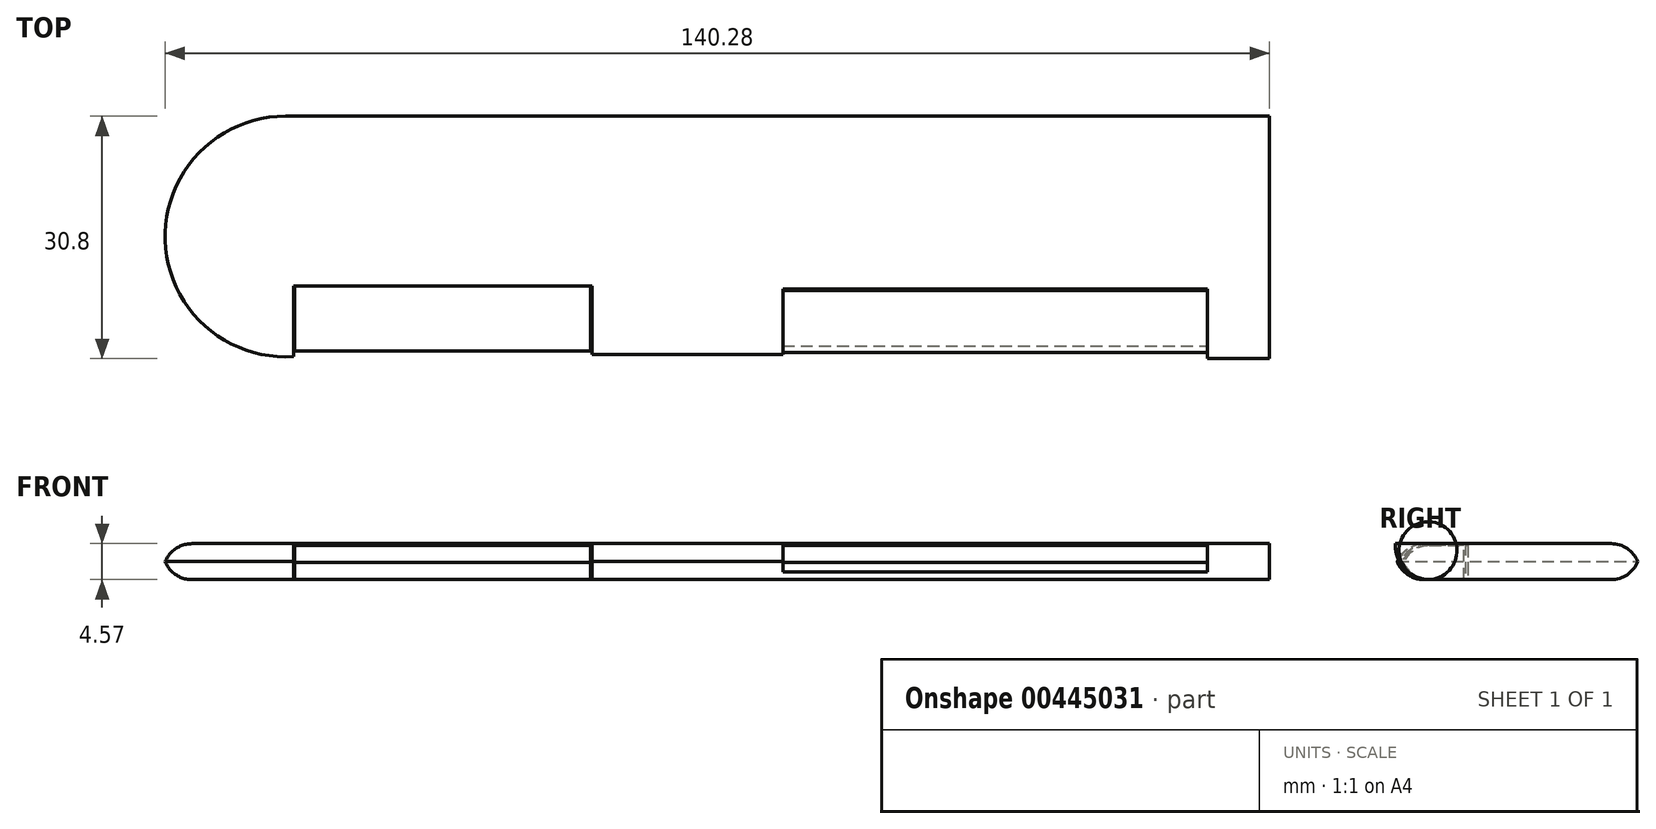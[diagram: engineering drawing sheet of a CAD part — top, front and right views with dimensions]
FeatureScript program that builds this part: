
annotation { "Feature Type Name" : "Feature", "Feature Type Description" : "" }
export const myFeature = defineFeature(function(context is Context, id is Id, definition is map)
    precondition{}
    {
        {
            var Q0;
            Q0=qCreatedBy(makeId("Top.planeOp"),FACE);
            var sketch = newSketch(context, id + "F0", { "sketchPlane" : qUnion([Q0])});
            skLineSegment(sketch, "E0", {"start": v(-60.57, 38.54) * mm, "end": v(53.16, 38.54) * mm});
            skLineSegment(sketch, "E1", {"start": v(53.16, 38.54) * mm, "end": v(53.16, 7.46) * mm});
            skLineSegment(sketch, "E2", {"start": v(53.16, 7.46) * mm, "end": v(45.3, 7.46) * mm});
            skLineSegment(sketch, "E3", {"start": v(45.3, 7.46) * mm, "end": v(45.3, 16.34) * mm});
            skLineSegment(sketch, "E4", {"start": v(45.3, 16.34) * mm, "end": v(-8.65, 16.34) * mm});
            skLineSegment(sketch, "E5", {"start": v(-8.65, 16.34) * mm, "end": v(-8.65, 7.46) * mm});
            skLineSegment(sketch, "E6", {"start": v(-8.65, 7.46) * mm, "end": v(-32.9, 7.46) * mm});
            skLineSegment(sketch, "E7", {"start": v(-32.9, 7.46) * mm, "end": v(-32.9, 16.68) * mm});
            skLineSegment(sketch, "E8", {"start": v(-32.9, 16.68) * mm, "end": v(-70.81, 16.68) * mm});
            skLineSegment(sketch, "E9", {"start": v(-70.81, 16.68) * mm, "end": v(-70.81, 7.46) * mm});
            skLineSegment(sketch, "E10", {"start": v(-60.57, 38.54) * mm, "end": v(-71.84, 38.54) * mm});
            skArc(sketch, "E11", {"start": v(-71.84, 38.54) * mm, "mid": v(-87.38, 22.47) * mm, "end": v(-70.81, 7.46) * mm});
            skSolve(sketch);
        }
        {
            var Q0;
            Q0 = qSketchRegion(id + "F0", true);
            extrude(context, id + "F1", {"entities" : qUnion([Q0]), "depth" : 4.57 * mm});
        }
        {
            var Q0;
            Q0=makeQuery(id+"F1.opExtrude","CAP_EDGE",EDGE,{"disambiguationData":[OSD([sQuery(id+"F0.wireOp",EDGE,"E0"),sQuery(id+"F0.wireOp",EDGE,"E10")])],"isStart":false});
            var Q1;
            Q1=makeQuery(id+"F1.opExtrude","CAP_EDGE",EDGE,{"disambiguationData":[OSD([sQuery(id+"F0.wireOp",EDGE,"E0"),sQuery(id+"F0.wireOp",EDGE,"E10")])],"isStart":true});
            fillet(context, id + "F2", {"entities" : qUnion([Q0, Q1]), "radius" : 3.68 * mm, "tangentPropagation" : true, "allowEdgeOverflow" : false});
        }
        {
            var Q0;
            Q0=qCreatedBy(makeId("Top.planeOp"),FACE);
            var sketch = newSketch(context, id + "F3", { "sketchPlane" : qUnion([Q0])});
            skLineSegment(sketch, "E12.bottom", {"start": v(-70.64, 8.12) * mm, "end": v(-33.07, 8.12) * mm});
            skLineSegment(sketch, "E12.top", {"start": v(-70.64, 16.85) * mm, "end": v(-33.07, 16.85) * mm});
            skLineSegment(sketch, "E12.left", {"start": v(-70.64, 8.12) * mm, "end": v(-70.64, 16.85) * mm});
            skLineSegment(sketch, "E12.right", {"start": v(-33.07, 8.12) * mm, "end": v(-33.07, 16.85) * mm});
            skLineSegment(sketch, "E13.bottom", {"start": v(-8.9, 7.92) * mm, "end": v(45.31, 7.92) * mm});
            skLineSegment(sketch, "E13.top", {"start": v(-8.9, 15.84) * mm, "end": v(45.31, 15.84) * mm});
            skLineSegment(sketch, "E13.left", {"start": v(-8.9, 7.92) * mm, "end": v(-8.9, 15.84) * mm});
            skLineSegment(sketch, "E13.right", {"start": v(45.31, 7.92) * mm, "end": v(45.31, 15.84) * mm});
            skSolve(sketch);
        }
        {
            var Q0;
            Q0=makeQuery(id+"F3.imprint","IMPRINT",FACE,{"disambiguationData":[TD([[makeQuery(id+"F3.imprint","IMPRINT",EDGE,{"derivedFrom":sQuery(id+"F3.wireOp",EDGE,"E12.bottom")}),1.0]])]});
            var Q1;
            Q1=makeQuery(id+"F3.imprint","IMPRINT",FACE,{"disambiguationData":[TD([[makeQuery(id+"F3.imprint","IMPRINT",EDGE,{"derivedFrom":sQuery(id+"F3.wireOp",EDGE,"E13.bottom")}),1.0]])]});
            extrude(context, id + "F4", {"entities" : qUnion([Q0, Q1]), "operationType" : NewBodyOperationType.ADD, "depth" : 4.32 * mm});
        }
        {
            var Q0;
            Q0=makeQuery(id+"F4.opExtrude","CAP_EDGE",EDGE,{"disambiguationData":[OSD([sQuery(id+"F3.wireOp",EDGE,"E12.bottom")])],"isStart":false});
            var Q1;
            Q1=makeQuery(id+"F4.opExtrude","CAP_EDGE",EDGE,{"disambiguationData":[OSD([sQuery(id+"F3.wireOp",EDGE,"E12.bottom")])],"isStart":true});
            var Q2;
            Q2=makeQuery(id+"F4.opExtrude","CAP_EDGE",EDGE,{"disambiguationData":[OSD([sQuery(id+"F3.wireOp",EDGE,"E13.bottom")])],"isStart":true});
            var Q3;
            Q3=makeQuery(id+"F4.opExtrude","CAP_EDGE",EDGE,{"disambiguationData":[OSD([sQuery(id+"F3.wireOp",EDGE,"E13.bottom")])],"isStart":false});
            fillet(context, id + "F5", {"entities" : qUnion([Q0, Q1, Q2, Q3]), "radius" : 3.68 * mm, "tangentPropagation" : true, "allowEdgeOverflow" : false});
        }
        {
            var Q0;
            Q0=makeQuery(id+"F1.opExtrude","CAP_EDGE",EDGE,{"disambiguationData":[OSD([sQuery(id+"F0.wireOp",EDGE,"E6")])],"isStart":true});
            var Q1;
            Q1=makeQuery(id+"F1.opExtrude","CAP_EDGE",EDGE,{"disambiguationData":[OSD([sQuery(id+"F0.wireOp",EDGE,"E6")])],"isStart":false});
            fillet(context, id + "F6", {"entities" : qUnion([Q0, Q1]), "radius" : 4.42 * mm, "tangentPropagation" : true, "allowEdgeOverflow" : false});
        }
        {
            var Q0;
            Q0=makeQuery(id+"F4.opExtrude","SWEPT_FACE",FACE,{"disambiguationData":[OSD([sQuery(id+"F3.wireOp",EDGE,"E13.top")])]});
            extrude(context, id + "F7", {"entities" : qUnion([Q0]), "operationType" : NewBodyOperationType.ADD, "depth" : 0.3 * mm});
        }
    });
